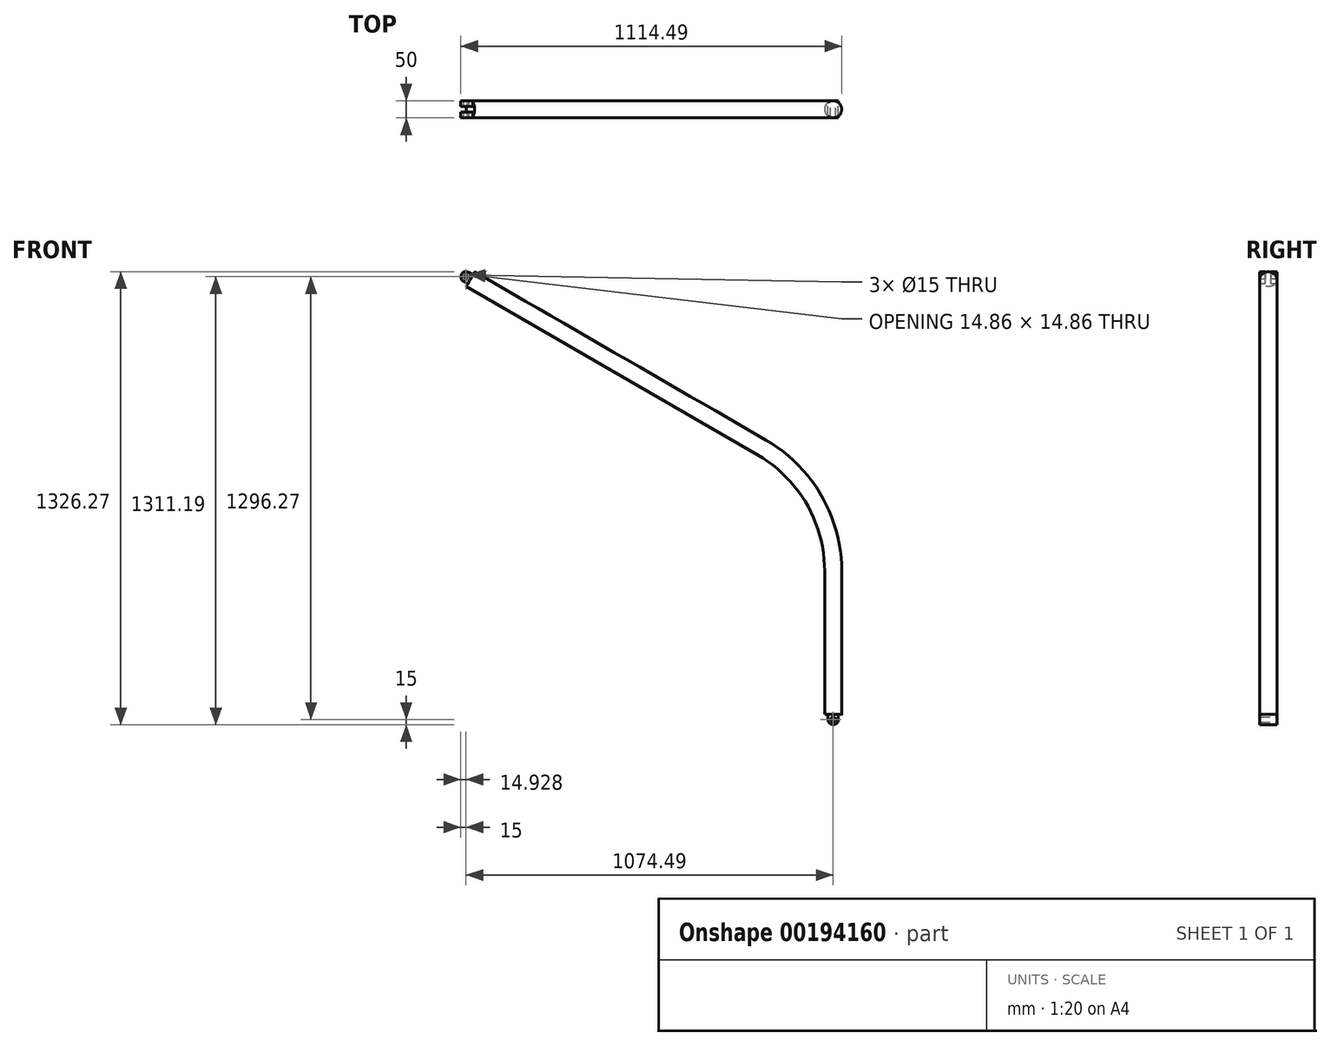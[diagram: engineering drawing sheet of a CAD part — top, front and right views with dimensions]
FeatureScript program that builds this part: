
annotation { "Feature Type Name" : "Feature", "Feature Type Description" : "" }
export const myFeature = defineFeature(function(context is Context, id is Id, definition is map)
    precondition{}
    {
        {
            var Q0;
            Q0=qCreatedBy(makeId("Front.planeOp"),FACE);
            var sketch = newSketch(context, id + "F0", { "sketchPlane" : qUnion([Q0])});
            skLineSegment(sketch, "E0.bottom", {"start": v(15, 0) * mm, "end": v(15, 0) * mm});
            skLineSegment(sketch, "E0.top", {"start": v(0, 30) * mm, "end": v(30, 30) * mm});
            skLineSegment(sketch, "E0.left", {"start": v(0, 15) * mm, "end": v(0, 30) * mm});
            skLineSegment(sketch, "E0.right", {"start": v(30, 15) * mm, "end": v(30, 30) * mm});
            skCircle(sketch, "E1", {"center": v(15, 15) * mm, "radius": 7.5 * mm});
            skPoint(sketch, "E2.visualSharp", {"position": v(30, 0) * mm});
            skArc(sketch, "E2.filletArc", {"start": v(15, 0) * mm, "mid": v(25.6, 4.4) * mm, "end": v(30, 15) * mm});
            skPoint(sketch, "E3.visualSharp", {"position": v(0, 0) * mm});
            skArc(sketch, "E3.filletArc", {"start": v(0, 15) * mm, "mid": v(4.4, 4.4) * mm, "end": v(15, 0) * mm});
            skSolve(sketch);
        }
        {
            var Q0;
            Q0=makeQuery(id+"F0.imprint","IMPRINT",FACE,{"disambiguationData":[TD([[makeQuery(id+"F0.imprint","IMPRINT",EDGE,{"derivedFrom":sQuery(id+"F0.wireOp",EDGE,"E0.top")}),-1.0]])]});
            extrude(context, id + "F1", {"entities" : qUnion([Q0]), "depth" : 25 * mm, "hasSecondDirection" : true, "secondDirectionOppositeDirection" : true, "secondDirectionDepth" : 25 * mm});
        }
        {
            var Q0;
            Q0=makeQuery(id+"F1.opExtrude","SWEPT_FACE",FACE,{"disambiguationData":[OSD([sQuery(id+"F0.wireOp",EDGE,"E0.top")])]});
            var sketch = newSketch(context, id + "F2", { "sketchPlane" : qUnion([Q0])});
            skCircle(sketch, "E4", {"center": v(15, 0) * mm, "radius": 25 * mm});
            skLineSegment(sketch, "E5", {"start": v(15, 25) * mm, "end": v(15, -25) * mm, "construction": true});
            skSolve(sketch);
        }
        {
            var Q0;
            Q0=qCreatedBy(makeId("Front.planeOp"),FACE);
            var sketch = newSketch(context, id + "F3", { "sketchPlane" : qUnion([Q0])});
            skLineSegment(sketch, "E6", {"start": v(15, 30) * mm, "end": v(15, 449) * mm});
            skArc(sketch, "E7", {"start": v(15, 449) * mm, "mid": v(-41.14, 658.5) * mm, "end": v(-194.5, 811.86) * mm});
            skLineSegment(sketch, "E8", {"start": v(15, 449) * mm, "end": v(-1249.53, 449) * mm, "construction": true});
            skLineSegment(sketch, "E9", {"start": v(-404, 868) * mm, "end": v(-404, -322.87) * mm, "construction": true});
            skLineSegment(sketch, "E10", {"start": v(-404, 449) * mm, "end": v(73.9, 1276.76) * mm, "construction": true});
            skLineSegment(sketch, "E11", {"start": v(-194.5, 811.86) * mm, "end": v(-1046.5, 1303.77) * mm});
            skPoint(sketch, "E12", {"position": v(15, 15) * mm});
            skSolve(sketch);
        }
        {
            var Q0;
            {var subQ0=sQuery(id+"F2.wireOp",EDGE,"E4");var subQ1=makeQuery(id+"F1.opExtrude","SWEPT_EDGE",EDGE,{"disambiguationData":[OSD([sQuery(id+"F0.wireOp",EDGE,"E0.top"),sQuery(id+"F0.wireOp",EDGE,"E0.right")])]});var subQ2=makeQuery(id+"F2.imprint","INTERSECT",VERTEX,{"disambiguationData":[OD(0.0)],"derivedFrom":[subQ1,subQ0]});Q0=makeQuery(id+"F2.imprint","IMPRINT",FACE,{"disambiguationData":[TD([[makeQuery(id+"F2.imprint","IMPRINT",EDGE,{"disambiguationData":[TD([[subQ2,1.0]])],"derivedFrom":subQ0}),1.0]])]});}
            var Q1;
            {var subQ0=sQuery(id+"F2.wireOp",EDGE,"E4");var subQ1=sQuery(id+"F0.wireOp",EDGE,"E0.top");var subQ2=makeQuery(id+"F1.opExtrude","SWEPT_EDGE",EDGE,{"disambiguationData":[OSD([subQ1,sQuery(id+"F0.wireOp",EDGE,"E0.left")])]});var subQ3=makeQuery(id+"F2.imprint","INTERSECT",VERTEX,{"disambiguationData":[OD(0.0)],"derivedFrom":[subQ2,subQ0]});Q1=makeQuery(id+"F2.imprint","IMPRINT",FACE,{"disambiguationData":[TD([[makeQuery(id+"F2.imprint","IMPRINT",EDGE,{"disambiguationData":[TD([[subQ3,1.0]])],"derivedFrom":subQ0}),1.0]])]});}
            var Q2;
            {var subQ0=sQuery(id+"F2.wireOp",EDGE,"E4");var subQ1=makeQuery(id+"F1.opExtrude","SWEPT_EDGE",EDGE,{"disambiguationData":[OSD([sQuery(id+"F0.wireOp",EDGE,"E0.top"),sQuery(id+"F0.wireOp",EDGE,"E0.left")])]});var subQ2=makeQuery(id+"F2.imprint","INTERSECT",VERTEX,{"disambiguationData":[OD(0.0)],"derivedFrom":[subQ1,subQ0]});Q2=makeQuery(id+"F2.imprint","IMPRINT",FACE,{"disambiguationData":[TD([[makeQuery(id+"F2.imprint","IMPRINT",EDGE,{"disambiguationData":[TD([[subQ2,-1.0]])],"derivedFrom":subQ0}),1.0]])]});}
            var Q3;
            Q3=sQuery(id+"F3.wireOp",EDGE,"E6");
            var Q4;
            Q4=sQuery(id+"F3.wireOp",EDGE,"E7");
            var Q5;
            Q5=sQuery(id+"F3.wireOp",EDGE,"E11");
            sweep(context, id + "F4", {"operationType" : NewBodyOperationType.ADD, "profiles" : qUnion([Q0, Q1, Q2]), "path" : qUnion([Q3, Q4, Q5])});
        }
        {
            var Q0;
            Q0=makeQuery(id+"F4.opSweep","CAP_FACE",FACE,{"disambiguationData":[OSD([sQuery(id+"F2.wireOp",EDGE,"E4"),sQuery(id+"F3.wireOp",VERTEX,"E11.end")])],"isStart":false});
            var sketch = newSketch(context, id + "F5", { "sketchPlane" : qUnion([Q0])});
            skLineSegment(sketch, "E13", {"start": v(139.41, 605.85) * mm, "end": v(-153.61, 605.85) * mm, "construction": true});
            skLineSegment(sketch, "E14", {"start": v(0, 710.64) * mm, "end": v(0, 486.63) * mm, "construction": true});
            skLineSegment(sketch, "E15.bottom", {"start": v(-25, 620.85) * mm, "end": v(25, 620.85) * mm});
            skLineSegment(sketch, "E15.top", {"start": v(-25, 590.85) * mm, "end": v(25, 590.85) * mm});
            skLineSegment(sketch, "E15.left", {"start": v(-25, 620.85) * mm, "end": v(-25, 590.85) * mm});
            skLineSegment(sketch, "E15.right", {"start": v(25, 620.85) * mm, "end": v(25, 590.85) * mm});
            skSolve(sketch);
        }
        {
            var Q0;
            {var subQ0=sQuery(id+"F5.wireOp",EDGE,"E15.left");var subQ1=sQuery(id+"F5.wireOp",EDGE,"E15.bottom");var subQ2=makeQuery(id+"F5.imprint","INTERSECT",VERTEX,{"derivedFrom":[subQ1,subQ0]});Q0=makeQuery(id+"F5.imprint","IMPRINT",FACE,{"disambiguationData":[TD([[makeQuery(id+"F5.imprint","IMPRINT",EDGE,{"disambiguationData":[TD([[subQ2,-1.0]])],"derivedFrom":subQ1}),-1.0]])]});}
            var Q1;
            {var subQ0=sQuery(id+"F5.wireOp",EDGE,"E15.bottom");var subQ1=makeQuery(id+"F4.opSweep","CAP_EDGE",EDGE,{"disambiguationData":[OSD([sQuery(id+"F2.wireOp",EDGE,"E4"),sQuery(id+"F3.wireOp",VERTEX,"E11.end")])],"isStart":false});var subQ2=makeQuery(id+"F5.imprint","INTERSECT",VERTEX,{"disambiguationData":[OD(0.0)],"derivedFrom":[subQ1,subQ0]});Q1=makeQuery(id+"F5.imprint","IMPRINT",FACE,{"disambiguationData":[TD([[makeQuery(id+"F5.imprint","IMPRINT",EDGE,{"disambiguationData":[TD([[subQ2,-1.0]])],"derivedFrom":subQ0}),-1.0]])]});}
            var Q2;
            {var subQ0=sQuery(id+"F5.wireOp",EDGE,"E15.left");var subQ1=sQuery(id+"F5.wireOp",EDGE,"E15.top");var subQ2=makeQuery(id+"F5.imprint","INTERSECT",VERTEX,{"derivedFrom":[subQ1,subQ0]});Q2=makeQuery(id+"F5.imprint","IMPRINT",FACE,{"disambiguationData":[TD([[makeQuery(id+"F5.imprint","IMPRINT",EDGE,{"disambiguationData":[TD([[subQ2,-1.0]])],"derivedFrom":subQ1}),1.0]])]});}
            var Q3;
            {var subQ0=sQuery(id+"F5.wireOp",EDGE,"E15.right");var subQ1=sQuery(id+"F5.wireOp",EDGE,"E15.top");var subQ2=makeQuery(id+"F5.imprint","INTERSECT",VERTEX,{"derivedFrom":[subQ1,subQ0]});Q3=makeQuery(id+"F5.imprint","IMPRINT",FACE,{"disambiguationData":[TD([[makeQuery(id+"F5.imprint","IMPRINT",EDGE,{"disambiguationData":[TD([[subQ2,1.0]])],"derivedFrom":subQ1}),1.0]])]});}
            var Q4;
            {var subQ0=sQuery(id+"F5.wireOp",EDGE,"E15.right");var subQ1=sQuery(id+"F5.wireOp",EDGE,"E15.bottom");var subQ2=makeQuery(id+"F5.imprint","INTERSECT",VERTEX,{"derivedFrom":[subQ1,subQ0]});Q4=makeQuery(id+"F5.imprint","IMPRINT",FACE,{"disambiguationData":[TD([[makeQuery(id+"F5.imprint","IMPRINT",EDGE,{"disambiguationData":[TD([[subQ2,1.0]])],"derivedFrom":subQ1}),-1.0]])]});}
            extrude(context, id + "F6", {"entities" : qUnion([Q0, Q1, Q2, Q3, Q4]), "operationType" : NewBodyOperationType.ADD, "depth" : 30 * mm});
        }
        {
            var Q0;
            Q0=makeQuery(id+"F6.opExtrude","CAP_EDGE",EDGE,{"disambiguationData":[OSD([sQuery(id+"F5.wireOp",EDGE,"E15.bottom")])],"isStart":false});
            var Q1;
            Q1=makeQuery(id+"F6.opExtrude","CAP_EDGE",EDGE,{"disambiguationData":[OSD([sQuery(id+"F5.wireOp",EDGE,"E15.top")])],"isStart":false});
            fillet(context, id + "F7", {"entities" : qUnion([Q0, Q1]), "radius" : 15 * mm, "tangentPropagation" : true, "allowEdgeOverflow" : false});
        }
        {
            var Q0;
            Q0=makeQuery(id+"F6.opExtrude","SWEPT_FACE",FACE,{"disambiguationData":[OSD([sQuery(id+"F5.wireOp",EDGE,"E15.right")])]});
            var sketch = newSketch(context, id + "F8", { "sketchPlane" : qUnion([Q0])});
            skCircle(sketch, "E16", {"center": v(-1059.5, 1311.27) * mm, "radius": 7.5 * mm});
            skPoint(sketch, "E17", {"position": v(15, 15) * mm});
            skSolve(sketch);
        }
        {
            var Q0;
            Q0=makeQuery(id+"F8.imprint","IMPRINT",FACE,{"disambiguationData":[TD([[makeQuery(id+"F8.imprint","IMPRINT",EDGE,{"derivedFrom":sQuery(id+"F8.wireOp",EDGE,"E16")}),1.0]])]});
            extrude(context, id + "F9", {"entities" : qUnion([Q0]), "operationType" : NewBodyOperationType.REMOVE, "oppositeDirection" : true, "depth" : 50 * mm});
        }
        {
            var Q0;
            Q0=makeQuery(id+"F6.opExtrude","SWEPT_FACE",FACE,{"disambiguationData":[OSD([sQuery(id+"F5.wireOp",EDGE,"E15.bottom")])]});
            var sketch = newSketch(context, id + "F10", { "sketchPlane" : qUnion([Q0])});
            skLineSegment(sketch, "E18.bottom", {"start": v(-1558.18, 8.33) * mm, "end": v(-1588.18, 8.33) * mm});
            skLineSegment(sketch, "E18.top", {"start": v(-1558.18, -8.33) * mm, "end": v(-1588.18, -8.33) * mm});
            skLineSegment(sketch, "E18.left", {"start": v(-1558.18, 8.33) * mm, "end": v(-1558.18, -8.33) * mm});
            skLineSegment(sketch, "E18.right", {"start": v(-1588.18, 8.33) * mm, "end": v(-1588.18, -8.33) * mm});
            skSolve(sketch);
        }
        {
            var Q0;
            {var subQ0=sQuery(id+"F10.wireOp",EDGE,"E18.right");Q0=makeQuery(id+"F10.imprint","IMPRINT",FACE,{"disambiguationData":[TD([[makeQuery(id+"F10.imprint","IMPRINT",EDGE,{"derivedFrom":subQ0}),1.0]])]});}
            var Q1;
            {var subQ0=sQuery(id+"F10.wireOp",EDGE,"E18.left");Q1=makeQuery(id+"F10.imprint","IMPRINT",FACE,{"disambiguationData":[TD([[makeQuery(id+"F10.imprint","IMPRINT",EDGE,{"derivedFrom":subQ0}),-1.0]])]});}
            extrude(context, id + "F11", {"entities" : qUnion([Q0, Q1]), "operationType" : NewBodyOperationType.REMOVE, "oppositeDirection" : true, "depth" : 30 * mm});
        }
    });
